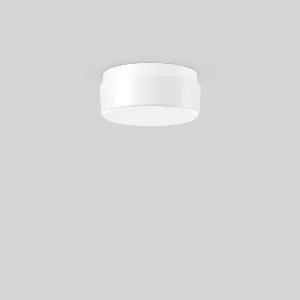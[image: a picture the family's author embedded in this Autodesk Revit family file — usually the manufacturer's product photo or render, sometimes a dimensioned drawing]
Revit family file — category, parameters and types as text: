
# Revit family: kreis_211416_002_13e0
name_source: partatom
category: Lighting Fixtures
units: mm (PartAtom-declared; Revit-internal decimal feet)

## family parameters
Cut with Voids When Loaded = No
Host = Face
Light Source = No
Part Type = Normal
Room Calculation Point = No
Round Connector Dimension = Use Diameter
Shared = No

## types (1)
- KREIS (1 x LED Modul 830, 1150 lm, 3000)
    Apparent Load = 12 VA
    CIE Flux Codes = 38 68 88 79 100
    Color Rendering = 80
    Color Temperature = 3000
    Default Elevation = 1800 mm
    Description = Series: KREIS
Round surface-mounted luminaire in classic design. Base: plastic. Opal glass: mouth-blown, satin finish. Diffuser fastening: spring system. Suitable for Ceiling mounting, Wall (surface). IP 43 ceiling mounting, IP 44 wall mounting. 
Colour: white
Diameter: 280 mm
Height: 120 mm
Lamp: LED exchangeable
Socket: without socket
Colour temperature: 3000K
Colour rendering index (CRI): 83
System power: 12 W
Rated luminous flux: 1150 lm
Luminous efficiency: 96 lm/W
Control gear: AC Strom, dim.Ph.an-/abschnitt
Protection class: I
Type of protection: IP 43
    Height = 120 mm
    Lamp = 1 x LED Modul 830
    Lamp Light Flux = 1150 lm
    Lamp count = 1
    Length = 280 mm
    Lifetime = 50000 h
    Luminous efficacy = 96 lm/W
    Manufacturer = RZB
    ModVariant = No
    Model = 211416.002
    Mounting Place = Ceiling, Wall
    Mounting Type = Surface mounted
    Number of Poles = 1
    OnlyDefault = Yes
    Power Factor = 1
    Product Name = KREIS
    Product group = Surface mounted ceiling and wall luminaires
    ProductGroupID = 305
    Protection Class = Protection class I
    Protection Degree = IP 43
    RLX_Detail_Level = 1
    RLX_Emergency_Light_Flux = 0 lm
    RLX_Emergency_Type = 0
    RLX_Emergency_Type_DB = No
    RlxData = <blob elided: 11641 chars, md5=e5468266>
    Socket = socket
    Standby Power = 0 W
    System Light Flux = 1150 lm
    System Power = 12 W
    Type Comments = Product without accessories
    Type Image = 21171.002.jpg
    URL = http://relux.com
    VarID = ---
    Voltage = 230 V
    Voltage Range = 220-240 V
    Weight = 0.00 kg
    Width = 0 mm  [stored 0 ft]

note: [stored X ft] marks values corroborated as IEEE doubles in the binary element streams (Revit-internal decimal feet)

## geometry (parser evidence)
native form markers: Sweep x13
no freeform markers — native parametric forms only
